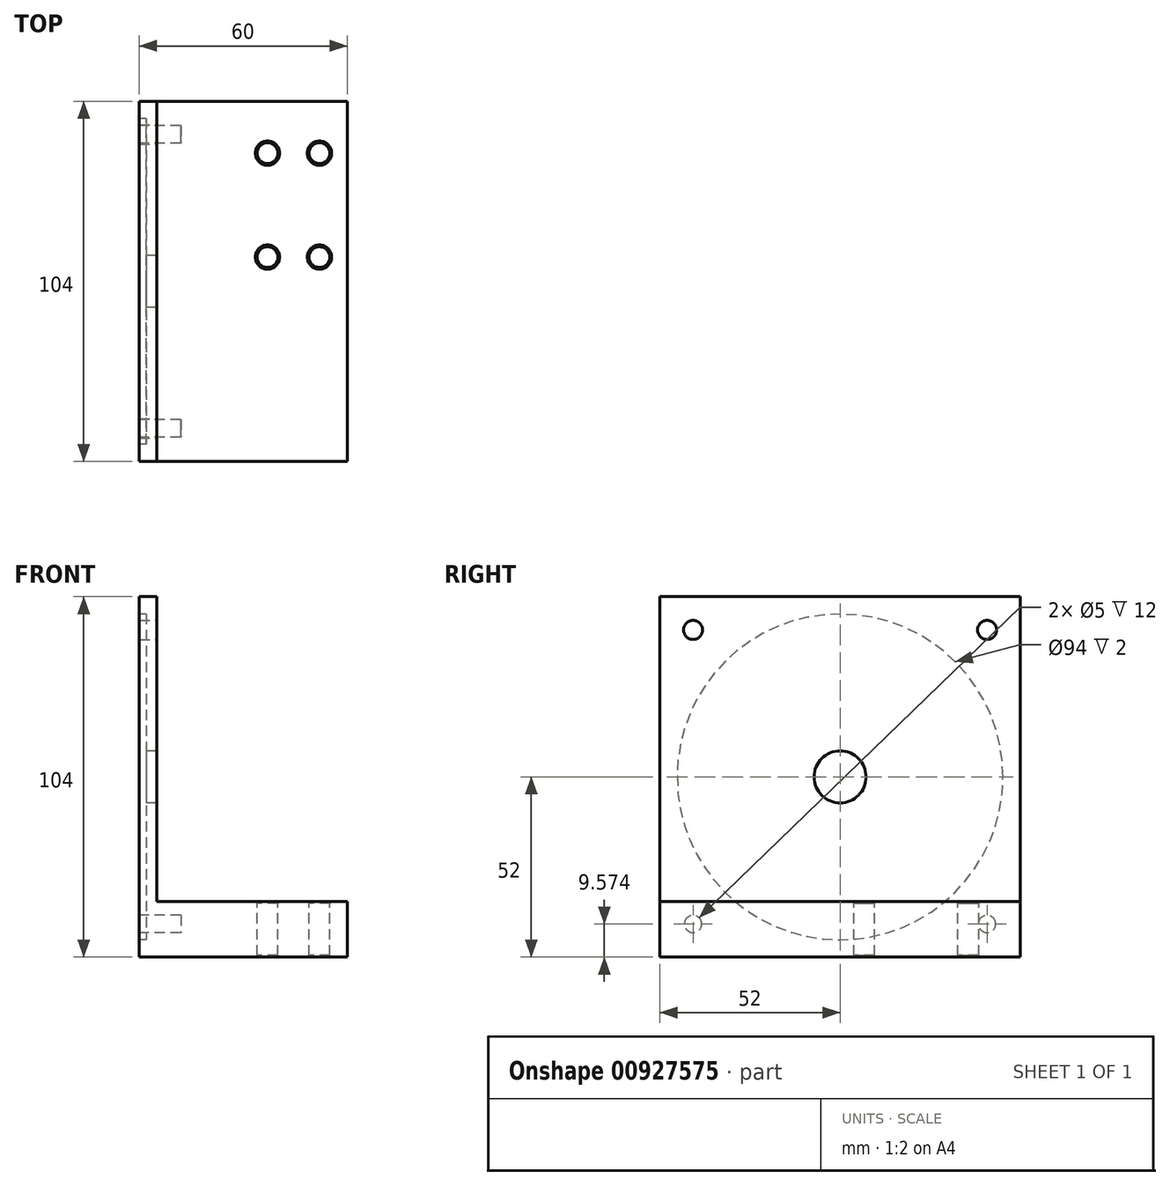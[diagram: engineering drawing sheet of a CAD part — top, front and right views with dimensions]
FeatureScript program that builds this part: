
annotation { "Feature Type Name" : "Feature", "Feature Type Description" : "" }
export const myFeature = defineFeature(function(context is Context, id is Id, definition is map)
    precondition{}
    {
        {
            var Q0;
            Q0=qCreatedBy(makeId("Right.planeOp"),FACE);
            var sketch = newSketch(context, id + "F0", { "sketchPlane" : qUnion([Q0])});
            skLineSegment(sketch, "E0.bottom", {"start": v(-52, -52) * mm, "end": v(52, -52) * mm});
            skLineSegment(sketch, "E0.top", {"start": v(-52, 52) * mm, "end": v(52, 52) * mm});
            skLineSegment(sketch, "E0.left", {"start": v(-52, -52) * mm, "end": v(-52, 52) * mm});
            skLineSegment(sketch, "E0.right", {"start": v(52, -52) * mm, "end": v(52, 52) * mm});
            skPoint(sketch, "E0.middle", {"position": v(0, 0) * mm});
            skSolve(sketch);
        }
        {
            var Q0;
            Q0 = qSketchRegion(id + "F0", true);
            extrude(context, id + "F1", {"entities" : qUnion([Q0]), "depth" : 5 * mm, "offsetDistance" : 25 * mm});
        }
        {
            var Q0;
            Q0=makeQuery(id+"F1.opExtrude","CAP_FACE",FACE,{"disambiguationData":[OSD([sQuery(id+"F0.wireOp",EDGE,"E0.bottom"),sQuery(id+"F0.wireOp",EDGE,"E0.top"),sQuery(id+"F0.wireOp",EDGE,"E0.left"),sQuery(id+"F0.wireOp",EDGE,"E0.right")])],"isStart":false});
            var sketch = newSketch(context, id + "F2", { "sketchPlane" : qUnion([Q0])});
            skLineSegment(sketch, "E1", {"start": v(-52, 52) * mm, "end": v(52, -52) * mm, "construction": true});
            skLineSegment(sketch, "E2", {"start": v(-52, -52) * mm, "end": v(52, 52) * mm, "construction": true});
            skCircle(sketch, "E3", {"center": v(42.43, 42.43) * mm, "radius": 2.75 * mm});
            skPoint(sketch, "E4", {"position": v(0, 0) * mm});
            skCircle(sketch, "E5.MirrorC", {"center": v(-42.43, 42.43) * mm, "radius": 2.75 * mm});
            skSolve(sketch);
        }
        {
            var Q0;
            Q0 = qSketchRegion(id + "F2", true);
            extrude(context, id + "F3", {"entities" : qUnion([Q0]), "operationType" : NewBodyOperationType.REMOVE, "endBound" : BoundingType.THROUGH_ALL, "oppositeDirection" : true, "depth" : 25 * mm, "offsetDistance" : 25 * mm});
        }
        {
            var Q0;
            Q0=makeQuery(id+"F1.opExtrude","CAP_FACE",FACE,{"disambiguationData":[OSD([sQuery(id+"F0.wireOp",EDGE,"E0.bottom"),sQuery(id+"F0.wireOp",EDGE,"E0.top"),sQuery(id+"F0.wireOp",EDGE,"E0.left"),sQuery(id+"F0.wireOp",EDGE,"E0.right")])],"isStart":false});
            var sketch = newSketch(context, id + "F4", { "sketchPlane" : qUnion([Q0])});
            skLineSegment(sketch, "E6.bottom", {"start": v(-52, -52) * mm, "end": v(52, -52) * mm});
            skLineSegment(sketch, "E6.top", {"start": v(-52, -36) * mm, "end": v(52, -36) * mm});
            skLineSegment(sketch, "E6.left", {"start": v(-52, -52) * mm, "end": v(-52, -36) * mm});
            skLineSegment(sketch, "E6.right", {"start": v(52, -52) * mm, "end": v(52, -36) * mm});
            skSolve(sketch);
        }
        {
            var Q0;
            Q0 = qSketchRegion(id + "F4", true);
            extrude(context, id + "F5", {"entities" : qUnion([Q0]), "operationType" : NewBodyOperationType.ADD, "depth" : 55 * mm, "offsetDistance" : 25 * mm});
        }
        {
            var Q0;
            Q0=makeQuery(id+"F1.opExtrude","CAP_FACE",FACE,{"disambiguationData":[OSD([sQuery(id+"F0.wireOp",EDGE,"E0.bottom"),sQuery(id+"F0.wireOp",EDGE,"E0.top"),sQuery(id+"F0.wireOp",EDGE,"E0.left"),sQuery(id+"F0.wireOp",EDGE,"E0.right")])],"isStart":true});
            var sketch = newSketch(context, id + "F6", { "sketchPlane" : qUnion([Q0])});
            skLineSegment(sketch, "E7", {"start": v(-52, 52) * mm, "end": v(52, -52) * mm, "construction": true});
            skLineSegment(sketch, "E8", {"start": v(52, 52) * mm, "end": v(-52, -52) * mm, "construction": true});
            skCircle(sketch, "E9", {"center": v(-42.43, -42.43) * mm, "radius": 2.5 * mm});
            skCircle(sketch, "E10.MirrorC", {"center": v(42.43, -42.43) * mm, "radius": 2.5 * mm});
            skSolve(sketch);
        }
        {
            var Q0;
            Q0 = qSketchRegion(id + "F6", true);
            extrude(context, id + "F7", {"entities" : qUnion([Q0]), "operationType" : NewBodyOperationType.REMOVE, "oppositeDirection" : true, "depth" : 12 * mm, "offsetDistance" : 25 * mm});
        }
        {
            var Q0;
            Q0=makeQuery(id+"F5.opExtrude","SWEPT_FACE",FACE,{"disambiguationData":[OSD([sQuery(id+"F4.wireOp",EDGE,"E6.top")])]});
            var sketch = newSketch(context, id + "F8", { "sketchPlane" : qUnion([Q0])});
            skPoint(sketch, "E11.startSnap0", {"position": v(32.5, 52) * mm});
            skPoint(sketch, "E11.endSnap0", {"position": v(32.5, -52) * mm});
            skLineSegment(sketch, "E12", {"start": v(52, 62.63) * mm, "end": v(52, -66.35) * mm, "construction": true});
            skLineSegment(sketch, "E13", {"start": v(37, 69.13) * mm, "end": v(37, -70.61) * mm, "construction": true});
            skCircle(sketch, "E14", {"center": v(52, 37) * mm, "radius": 3 * mm});
            skCircle(sketch, "E15", {"center": v(52, 7) * mm, "radius": 3 * mm});
            skCircle(sketch, "E16", {"center": v(37, 37) * mm, "radius": 3 * mm});
            skCircle(sketch, "E17", {"center": v(37, 7) * mm, "radius": 3 * mm});
            skSolve(sketch);
        }
        {
            var Q0;
            Q0=makeQuery(id+"F1.opExtrude","CAP_FACE",FACE,{"disambiguationData":[OSD([sQuery(id+"F0.wireOp",EDGE,"E0.bottom"),sQuery(id+"F0.wireOp",EDGE,"E0.top"),sQuery(id+"F0.wireOp",EDGE,"E0.left"),sQuery(id+"F0.wireOp",EDGE,"E0.right")])],"isStart":true});
            var sketch = newSketch(context, id + "F9", { "sketchPlane" : qUnion([Q0])});
            skCircle(sketch, "E18", {"center": v(0, 0) * mm, "radius": 47 * mm});
            skSolve(sketch);
        }
        {
            var Q0;
            Q0 = qSketchRegion(id + "F9", true);
            extrude(context, id + "F10", {"entities" : qUnion([Q0]), "operationType" : NewBodyOperationType.REMOVE, "oppositeDirection" : true, "depth" : 2 * mm, "offsetDistance" : 25 * mm});
        }
        {
            var Q0;
            Q0=makeQuery(id+"F10.boolean.opBoolean","COPY",FACE,{"derivedFrom":makeQuery(id+"F10.opExtrude","CAP_FACE",FACE,{"disambiguationData":[OSD([sQuery(id+"F9.wireOp",EDGE,"E18")])],"isStart":false})});
            var sketch = newSketch(context, id + "F11", { "sketchPlane" : qUnion([Q0])});
            skCircle(sketch, "E19", {"center": v(0, 0) * mm, "radius": 7.5 * mm});
            skSolve(sketch);
        }
        {
            var Q0;
            Q0 = qSketchRegion(id + "F11", true);
            extrude(context, id + "F12", {"entities" : qUnion([Q0]), "operationType" : NewBodyOperationType.REMOVE, "endBound" : BoundingType.THROUGH_ALL, "oppositeDirection" : true, "depth" : 25 * mm, "offsetDistance" : 25 * mm});
        }
        {
            var Q0;
            Q0 = qSketchRegion(id + "F8", true);
            extrude(context, id + "F13", {"entities" : qUnion([Q0]), "operationType" : NewBodyOperationType.REMOVE, "endBound" : BoundingType.THROUGH_ALL, "oppositeDirection" : true, "depth" : 25 * mm, "offsetDistance" : 25 * mm});
        }
        {
            var Q0;
            Q0=makeQuery(id+"F13.boolean.opBoolean","COPY",FACE,{"derivedFrom":makeQuery(id+"F13.opExtrude","SWEPT_FACE",FACE,{"disambiguationData":[OSD([sQuery(id+"F8.wireOp",EDGE,"E16")])]})});
            var Q1;
            Q1=makeQuery(id+"F13.boolean.opBoolean","COPY",FACE,{"derivedFrom":makeQuery(id+"F13.opExtrude","SWEPT_FACE",FACE,{"disambiguationData":[OSD([sQuery(id+"F8.wireOp",EDGE,"E14")])]})});
            var Q2;
            Q2=makeQuery(id+"F13.boolean.opBoolean","COPY",FACE,{"derivedFrom":makeQuery(id+"F13.opExtrude","SWEPT_FACE",FACE,{"disambiguationData":[OSD([sQuery(id+"F8.wireOp",EDGE,"E17")])]})});
            var Q3;
            Q3=makeQuery(id+"F13.boolean.opBoolean","COPY",FACE,{"derivedFrom":makeQuery(id+"F13.opExtrude","SWEPT_FACE",FACE,{"disambiguationData":[OSD([sQuery(id+"F8.wireOp",EDGE,"E15")])]})});
            chamfer(context, id + "F14", {"entities" : qUnion([Q0, Q1, Q2, Q3]), "width" : 0.5 * mm, "tangentPropagation" : true});
        }
    });
